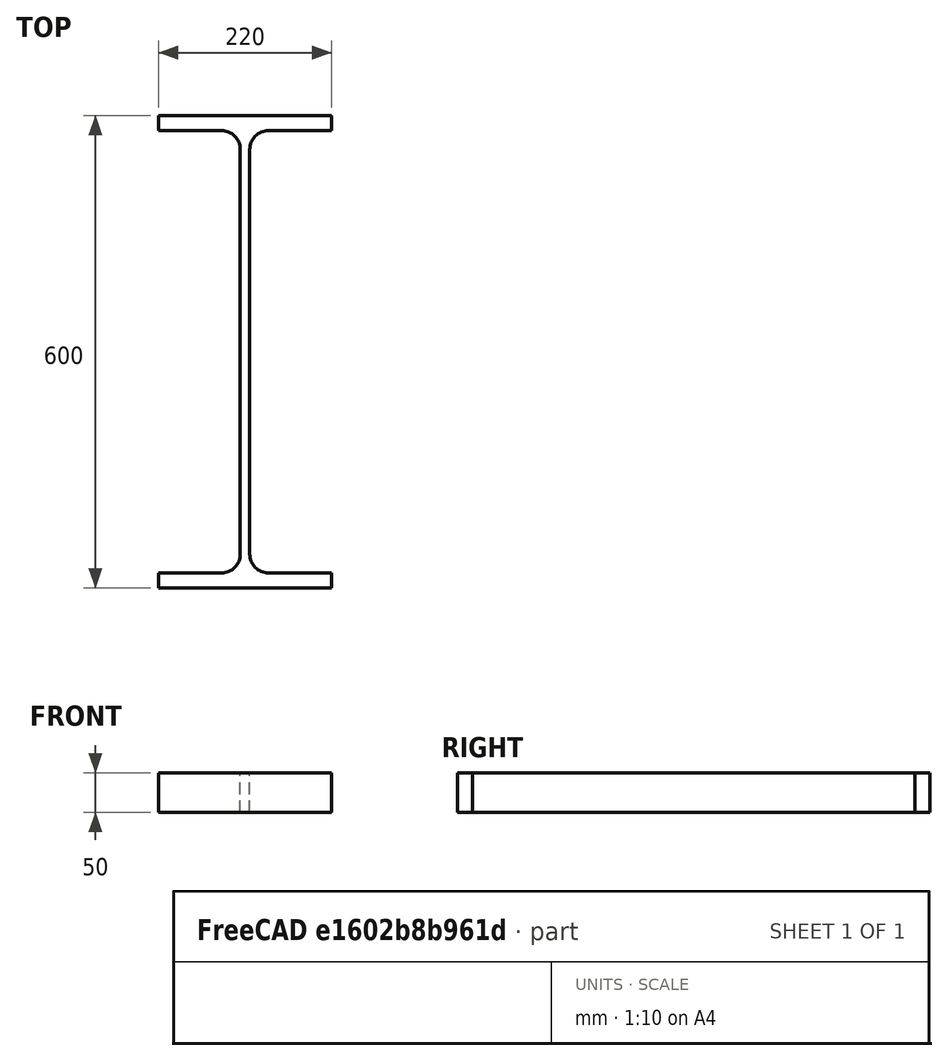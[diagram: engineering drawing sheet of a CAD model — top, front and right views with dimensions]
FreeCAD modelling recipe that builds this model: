
FCSTD DOCUMENT  (FreeCAD 0.15R4671 (Git))
Label: IPE-Profile 600 DIN1025-5 S235JR
License: All rights reserved
LicenseURL: http://en.wikipedia.org/wiki/All_rights_reserved
objects: Sketcher::SketchObject×1, Part::Extrusion×1
note: 2 computed .brp shape members not serialized (recipe doc carries the construction recipe); baked Part::Feature solids carry a one-line shape summary decoded from their .brp

FEATURE [Sketcher::SketchObject] Sketch
  sketch-geometry (16):
    g0: LineSegment StartX=6 StartY=-257 StartZ=0 EndX=6 EndY=257 EndZ=0
    g1: LineSegment StartX=30 StartY=281 StartZ=0 EndX=110 EndY=281 EndZ=0
    g2: LineSegment StartX=110 StartY=281 StartZ=0 EndX=110 EndY=300 EndZ=0
    g3: LineSegment StartX=110 StartY=300 StartZ=0 EndX=-110 EndY=300 EndZ=0
    g4: LineSegment StartX=-110 StartY=300 StartZ=0 EndX=-110 EndY=281 EndZ=0
    g5: LineSegment StartX=-110 StartY=281 StartZ=0 EndX=-30 EndY=281 EndZ=0
    g6: LineSegment StartX=-6 StartY=257 StartZ=0 EndX=-6 EndY=-257 EndZ=0
    g7: LineSegment StartX=-30 StartY=-281 StartZ=0 EndX=-110 EndY=-281 EndZ=0
    g8: LineSegment StartX=-110 StartY=-281 StartZ=0 EndX=-110 EndY=-300 EndZ=0
    g9: LineSegment StartX=-110 StartY=-300 StartZ=0 EndX=110 EndY=-300 EndZ=0
    g10: LineSegment StartX=110 StartY=-300 StartZ=0 EndX=110 EndY=-281 EndZ=0
    g11: LineSegment StartX=110 StartY=-281 StartZ=0 EndX=30 EndY=-281 EndZ=0
    g12: ArcOfCircle CenterX=30 CenterY=257 CenterZ=0 NormalX=0 NormalY=0 NormalZ=1 Radius=24 StartAngle=1.5708 EndAngle=3.14159
    g13: ArcOfCircle CenterX=30 CenterY=-257 CenterZ=0 NormalX=0 NormalY=0 NormalZ=1 Radius=24 StartAngle=3.14159 EndAngle=4.71239
    g14: ArcOfCircle CenterX=-30 CenterY=257 CenterZ=0 NormalX=0 NormalY=0 NormalZ=1 Radius=24 StartAngle=0 EndAngle=1.5708
    g15: ArcOfCircle CenterX=-30 CenterY=-257 CenterZ=0 NormalX=0 NormalY=0 NormalZ=1 Radius=24 StartAngle=4.71239 EndAngle=6.28319
  constraints (42):
    c: Vertical(g0)
    c: Coincident(g2,g1)
    c: Vertical(g2)
    c: Coincident(g3,g2)
    c: Coincident(g4,g3)
    c: Vertical(g4)
    c: Coincident(g5,g4)
    c: Horizontal(g5)
    c: Vertical(g6)
    c: Horizontal(g7)
    c: Coincident(g8,g7)
    c: Vertical(g8)
    c: Coincident(g9,g8)
    c: Horizontal(g9)
    c: Coincident(g10,g9)
    c: Vertical(g10)
    c: Coincident(g11,g10)
    c: Horizontal(g11)
    c: Tangent(g1,g12) = 1.5708
    c: Tangent(g0,g12) = 1.5708
    c: Tangent(g0,g13) = 1.5708
    c: Tangent(g11,g13) = 1.5708
    c: Tangent(g5,g14) = 1.5708
    c: Tangent(g6,g14) = 1.5708
    c: Tangent(g6,g15) = 1.5708
    c: Tangent(g7,g15) = 1.5708
    c: Equal(g3,g9)
    c: Equal(g2,g4)
    c: Equal(g4,g8)
    c: Equal(g8,g10)
    c: Equal(g12,g14)
    c: Equal(g14,g15)
    c: Equal(g15,g13)
    c: Symmetric(g2,g3,g-2)
    c: Symmetric(g9,g8,g-2)
    c: Symmetric(g0,g6,g-2)
    c: Symmetric(g2,g9,g-1)
    c: DistanceY(g2,g9) = -600
    c: DistanceX(g3) = -220
    c: DistanceX(g0,g6) = -12
    c: DistanceY(g2) = 19
    c: Radius(g12) = 24
FEATURE [Part::Extrusion] Extrude  label="IPE-Profile 600 DIN1025-5 S235JR"
  Base = -> Sketch
  Dir = (0,0,50)
  Solid = true
